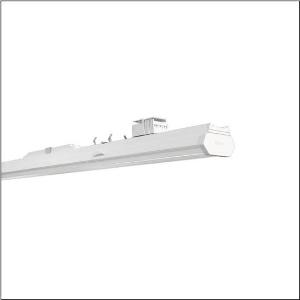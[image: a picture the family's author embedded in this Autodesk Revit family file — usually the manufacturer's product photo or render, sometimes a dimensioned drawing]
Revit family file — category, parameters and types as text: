
# Revit family: licross_r__21_protected_mo_52td1bcn485g_f119
name_source: partatom
category: Lighting Fixtures
units: mm (PartAtom-declared; Revit-internal decimal feet)

## family parameters
Cut with Voids When Loaded = No
Host = Face
Light Source = No
Part Type = Normal
Room Calculation Point = No
Round Connector Dimension = Use Diameter
Shared = No

## types (1)
- --- (1 x LED, 8570 lm, 50.4 W, 4000K)
    Apparent Load = 50 VA
    CIE Flux Codes = 54 82 95 97 100
    Color Rendering = 80
    Color Temperature = 4000K
    Default Elevation = 1800 mm
    Description = Licross® 21 Protected MO, luminaire insert, of sheet steel, galvanised, coil coated, white, length: 1.500mm, width: 90mm, height: 103mm, LED rated luminous flux: 8.570lm, light colour: 840, SDCM (Standard Deviation of Colour Matching)MacAdam ≤ 3 SDCM (initial), control gear: ON/OFF Multilumen, CLOi, with plug, 3-pole, with phase selection, mains connection: 220..240V, AC, 50/60Hz, start of lifetime: 50W, end of service life: 61W, internal wiring halogen-free, primary optical cover: cover, of PMMA, light emission: direct distribution, primary light characteristic: symmetric, protection rating (complete): IP54, insulation class (complete): insulation class I (protective earthing), certification: CE, ENEC, VDE, UKCA, protection symbol: D if used in an environment with non-conductive dust loads with corresponding accessories, impact resistance: IK06, permissible ambient temperature for indoor applications: -35..+45°C, corresponds to IFS (International Featured Standards) requirements for safety and quality in the food industry, reducing of maximum allowable ambient temperature of 5°C with ceiling mounting, LABS conformity tested according to VDMA 24364:2018-05, packaging unit: 1 piece
    Height = 92 mm
    Lamp = 1 x LED
    Lamp Light Flux = 8570 lm
    Lamp Power = 50.4 W
    Lamp count = 1
    Length = 1500 mm
    Luminous efficacy = 170 lm/W
    Manufacturer = Siteco
    ModVariant = No
    Model = 52TD1BCN485G
    Mounting Place = Ceiling
    Mounting Type = Pendant
    Number of Poles = 1
    OnlyDefault = Yes
    Power Factor = 1
    Product Name = Licross® 21 Protected MO
    Product group = luminaire insert | ceiling pendant
    ProductGroupID = 901
    Protection Class = Protection class I
    Protection Degree = IP 54
    RLX_Detail_Level = 1
    RLX_Emergency_Light_Flux = 0 lm
    RLX_Emergency_Type = 0
    RLX_Emergency_Type_DB = No
    RlxData = <blob elided: 22081 chars, md5=d86835dc>
    Socket = socket
    Standby Power = 0 W
    System Light Flux = 8570 lm
    System Power = 50 W
    Type Comments = factory setting: luminous flux: 100 % | (A | C | E) | 117 mA
    Type Image = l_1256148.jpg
    URL = http://relux.com
    VarID = @adj_115423
    Voltage = 0 V
    Weight = 0.00 kg
    Width = 88 mm

## geometry (parser evidence)
native form markers: Blend x4, Sweep x11
no freeform markers — native parametric forms only
